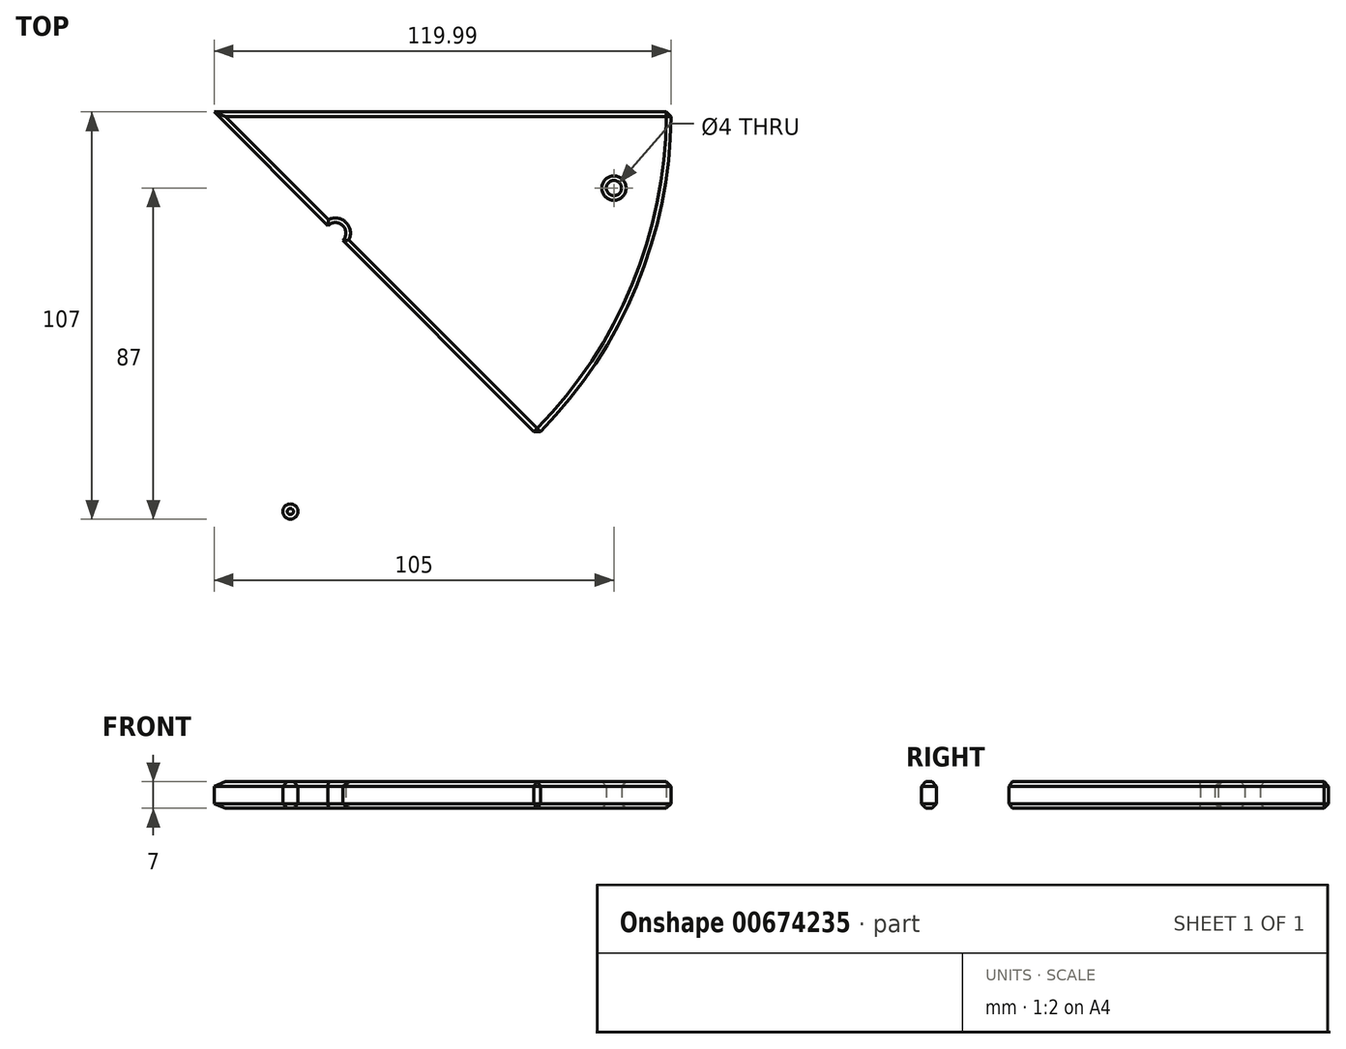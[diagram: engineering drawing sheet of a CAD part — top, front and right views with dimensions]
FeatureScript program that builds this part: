
annotation { "Feature Type Name" : "Feature", "Feature Type Description" : "" }
export const myFeature = defineFeature(function(context is Context, id is Id, definition is map)
    precondition{}
    {
        {
            var Q0;
            Q0=qCreatedBy(makeId("Top.planeOp"),FACE);
            var sketch = newSketch(context, id + "F0", { "sketchPlane" : qUnion([Q0])});
            skArc(sketch, "E0", {"start": v(0, -120) * mm, "mid": v(84.85, -84.85) * mm, "end": v(120, 0) * mm});
            skLineSegment(sketch, "E1", {"start": v(0, 0) * mm, "end": v(120, 0) * mm});
            skLineSegment(sketch, "E2", {"start": v(0, 0) * mm, "end": v(0, -120) * mm});
            skSolve(sketch);
        }
        {
            var Q0;
            Q0 = qSketchRegion(id + "F0", true);
            extrude(context, id + "F1", {"entities" : qUnion([Q0]), "depth" : 7 * mm, "offsetDistance" : 25 * mm});
        }
        {
            var Q0;
            Q0=qCreatedBy(makeId("Top.planeOp"),FACE);
            var sketch = newSketch(context, id + "F2", { "sketchPlane" : qUnion([Q0])});
            skLineSegment(sketch, "E3.0.0", {"start": v(120, 0) * mm, "end": v(0, 0) * mm});
            skLineSegment(sketch, "E3.0.1", {"start": v(0, 0) * mm, "end": v(0, -120) * mm});
            skArc(sketch, "E3.0.2", {"start": v(0, -120) * mm, "mid": v(84.85, -84.85) * mm, "end": v(120, 0) * mm});
            skLineSegment(sketch, "E4", {"start": v(0, 0) * mm, "end": v(84.85, -84.85) * mm});
            skCircle(sketch, "E5", {"center": v(31.82, -31.82) * mm, "radius": 2.75 * mm});
            skCircle(sketch, "E6", {"center": v(105, -20) * mm, "radius": 2 * mm});
            skLineSegment(sketch, "E7", {"start": v(105, -20) * mm, "end": v(105, 0) * mm, "construction": true});
            skCircle(sketch, "E8.MirrorC", {"center": v(20, -105) * mm, "radius": 2 * mm});
            skSolve(sketch);
        }
        {
            var Q0;
            Q0=makeQuery(id+"F2.imprint","IMPRINT",FACE,{"disambiguationData":[TD([[makeQuery(id+"F2.imprint","IMPRINT",EDGE,{"derivedFrom":sQuery(id+"F2.wireOp",EDGE,"E5")}),1.0]])]});
            var Q1;
            Q1=makeQuery(id+"F2.imprint","IMPRINT",FACE,{"disambiguationData":[TD([[makeQuery(id+"F2.imprint","IMPRINT",EDGE,{"derivedFrom":sQuery(id+"F2.wireOp",EDGE,"E8.MirrorC")}),-1.0]])]});
            var Q2;
            Q2=makeQuery(id+"F2.imprint","IMPRINT",FACE,{"disambiguationData":[TD([[makeQuery(id+"F2.imprint","IMPRINT",EDGE,{"derivedFrom":sQuery(id+"F2.wireOp",EDGE,"E6")}),1.0]])]});
            extrude(context, id + "F3", {"entities" : qUnion([Q0, Q1, Q2]), "operationType" : NewBodyOperationType.REMOVE, "endBound" : BoundingType.THROUGH_ALL, "depth" : 25 * mm, "offsetDistance" : 25 * mm});
        }
        {
            var Q0;
            Q0=makeQuery(id+"F1.opExtrude","CAP_FACE",FACE,{"disambiguationData":[OSD([sQuery(id+"F0.wireOp",EDGE,"E0"),sQuery(id+"F0.wireOp",EDGE,"E1"),sQuery(id+"F0.wireOp",EDGE,"E2")])],"isStart":false});
            var Q1;
            Q1=makeQuery(id+"F1.opExtrude","CAP_FACE",FACE,{"disambiguationData":[OSD([sQuery(id+"F0.wireOp",EDGE,"E0"),sQuery(id+"F0.wireOp",EDGE,"E1"),sQuery(id+"F0.wireOp",EDGE,"E2")])],"isStart":true});
            var Q2;
            Q2=makeQuery(id+"F1.opExtrude","SWEPT_FACE",FACE,{"disambiguationData":[OSD([sQuery(id+"F0.wireOp",EDGE,"E0")])]});
            chamfer(context, id + "F4", {"entities" : qUnion([Q0, Q1, Q2]), "width" : 1.2 * mm, "tangentPropagation" : true});
        }
    });
